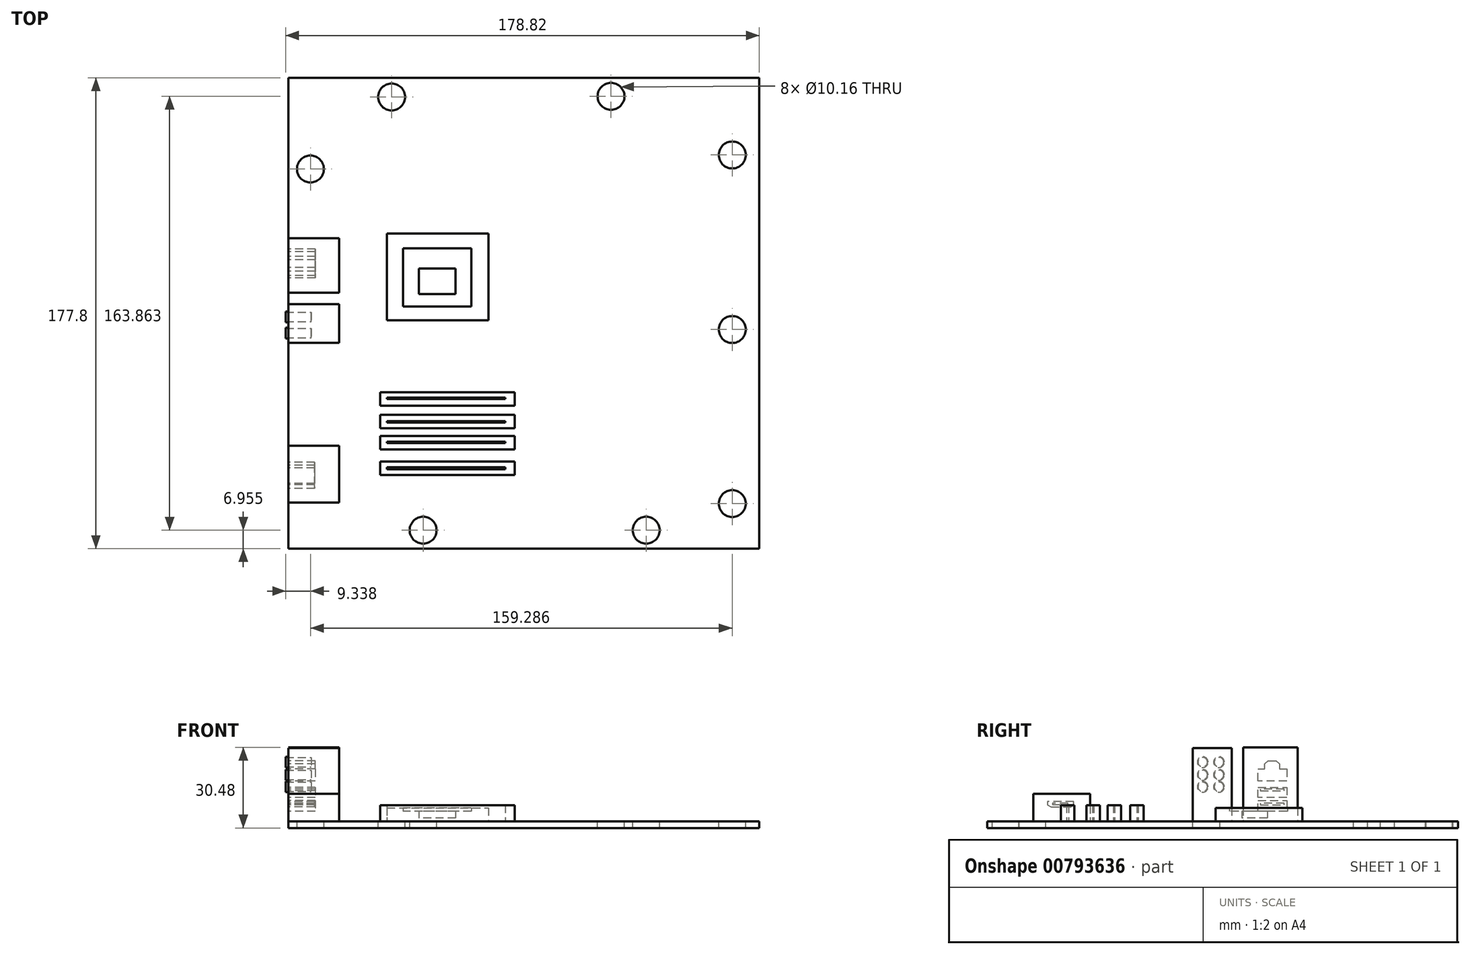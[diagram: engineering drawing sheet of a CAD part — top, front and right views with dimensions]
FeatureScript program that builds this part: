
annotation { "Feature Type Name" : "Feature", "Feature Type Description" : "" }
export const myFeature = defineFeature(function(context is Context, id is Id, definition is map)
    precondition{}
    {
        {
            var Q0;
            Q0=qCreatedBy(makeId("Top.planeOp"),FACE);
            var sketch = newSketch(context, id + "F0", { "sketchPlane" : qUnion([Q0])});
            skLineSegment(sketch, "E0", {"start": v(0, 177.8) * mm, "end": v(0, 0) * mm});
            skLineSegment(sketch, "E1", {"start": v(0, 0) * mm, "end": v(177.8, 0) * mm});
            skLineSegment(sketch, "E2", {"start": v(177.8, 0) * mm, "end": v(177.8, 177.8) * mm});
            skLineSegment(sketch, "E3", {"start": v(177.8, 177.8) * mm, "end": v(0, 177.8) * mm});
            skSolve(sketch);
        }
        {
            var Q0;
            Q0=makeQuery(id+"F0.imprint","IMPRINT",FACE,{"disambiguationData":[TD([[makeQuery(id+"F0.imprint","IMPRINT",EDGE,{"derivedFrom":sQuery(id+"F0.wireOp",EDGE,"E0")}),1.0]])]});
            extrude(context, id + "F1", {"entities" : qUnion([Q0]), "oppositeDirection" : true, "depth" : 2.54 * mm, "offsetDistance" : 25.4 * mm});
        }
        {
            var Q0;
            Q0=makeQuery(id+"F1.opExtrude","CAP_FACE",FACE,{"disambiguationData":[OSD([sQuery(id+"F0.wireOp",EDGE,"E0"),sQuery(id+"F0.wireOp",EDGE,"E1"),sQuery(id+"F0.wireOp",EDGE,"E2"),sQuery(id+"F0.wireOp",EDGE,"E3")])],"isStart":true});
            var sketch = newSketch(context, id + "F2", { "sketchPlane" : qUnion([Q0])});
            skLineSegment(sketch, "E4", {"start": v(0, 96.61) * mm, "end": v(0, 117.26) * mm});
            skLineSegment(sketch, "E5", {"start": v(0, 117.26) * mm, "end": v(19.18, 117.26) * mm});
            skLineSegment(sketch, "E6", {"start": v(19.18, 117.26) * mm, "end": v(19.18, 96.61) * mm});
            skLineSegment(sketch, "E7", {"start": v(19.18, 96.61) * mm, "end": v(0, 96.61) * mm});
            skSolve(sketch);
        }
        {
            var Q0;
            Q0 = qSketchRegion(id + "F2", true);
            extrude(context, id + "F3", {"entities" : qUnion([Q0]), "operationType" : NewBodyOperationType.ADD, "depth" : 27.94 * mm, "offsetDistance" : 25.4 * mm});
        }
        {
            var Q0;
            Q0=makeQuery(id+"F3.boolean.opBoolean","MERGE",FACE,{"derivedFrom":[makeQuery(id+"F1.opExtrude","SWEPT_FACE",FACE,{"disambiguationData":[OSD([sQuery(id+"F0.wireOp",EDGE,"E0")])]}),makeQuery(id+"F3.opExtrude","SWEPT_FACE",FACE,{"disambiguationData":[OSD([sQuery(id+"F2.wireOp",EDGE,"E4")])]})]});
            var sketch = newSketch(context, id + "F4", { "sketchPlane" : qUnion([Q0])});
            skLineSegment(sketch, "E8", {"start": v(-113.13, 3.74) * mm, "end": v(-102.3, 3.74) * mm});
            skLineSegment(sketch, "E9", {"start": v(-102.3, 3.74) * mm, "end": v(-102.3, 7.88) * mm});
            skLineSegment(sketch, "E10", {"start": v(-102.3, 7.88) * mm, "end": v(-113.13, 7.88) * mm});
            skLineSegment(sketch, "E11", {"start": v(-113.13, 7.88) * mm, "end": v(-113.13, 3.74) * mm});
            skLineSegment(sketch, "E12", {"start": v(-112.13, 6.81) * mm, "end": v(-103.18, 6.81) * mm});
            skLineSegment(sketch, "E13", {"start": v(-103.18, 6.81) * mm, "end": v(-103.18, 6.2) * mm});
            skLineSegment(sketch, "E14", {"start": v(-103.18, 6.2) * mm, "end": v(-112.13, 6.2) * mm});
            skLineSegment(sketch, "E15", {"start": v(-112.13, 6.2) * mm, "end": v(-112.13, 6.81) * mm});
            skLineSegment(sketch, "E16", {"start": v(-113.13, 8.95) * mm, "end": v(-102.3, 8.95) * mm});
            skLineSegment(sketch, "E17", {"start": v(-102.3, 8.95) * mm, "end": v(-102.3, 12.82) * mm});
            skLineSegment(sketch, "E18", {"start": v(-102.3, 12.82) * mm, "end": v(-113.13, 12.82) * mm});
            skLineSegment(sketch, "E19", {"start": v(-113.13, 12.82) * mm, "end": v(-113.13, 8.95) * mm});
            skLineSegment(sketch, "E20", {"start": v(-112.13, 12.1) * mm, "end": v(-103.18, 12.1) * mm});
            skPoint(sketch, "E20.endSnap0", {"position": v(-103.18, 6.5) * mm});
            skLineSegment(sketch, "E21", {"start": v(-103.18, 12.1) * mm, "end": v(-103.18, 11.52) * mm});
            skLineSegment(sketch, "E22", {"start": v(-103.18, 11.52) * mm, "end": v(-112.13, 11.52) * mm});
            skLineSegment(sketch, "E23", {"start": v(-112.13, 11.52) * mm, "end": v(-112.13, 12.1) * mm});
            skLineSegment(sketch, "E24", {"start": v(-113.13, 15.2) * mm, "end": v(-102.3, 15.2) * mm});
            skLineSegment(sketch, "E25", {"start": v(-102.3, 15.2) * mm, "end": v(-102.3, 19.75) * mm});
            skLineSegment(sketch, "E26", {"start": v(-102.3, 19.75) * mm, "end": v(-104.74, 19.75) * mm});
            skLineSegment(sketch, "E27", {"start": v(-104.74, 19.75) * mm, "end": v(-104.74, 21.69) * mm});
            skLineSegment(sketch, "E28", {"start": v(-104.74, 21.69) * mm, "end": v(-106.12, 22.8) * mm});
            skLineSegment(sketch, "E29", {"start": v(-106.12, 22.8) * mm, "end": v(-109.16, 22.8) * mm});
            skLineSegment(sketch, "E30", {"start": v(-109.16, 22.8) * mm, "end": v(-110.4, 21.69) * mm});
            skLineSegment(sketch, "E31", {"start": v(-110.4, 21.69) * mm, "end": v(-110.4, 19.75) * mm});
            skLineSegment(sketch, "E32", {"start": v(-110.4, 19.75) * mm, "end": v(-113.13, 19.75) * mm});
            skLineSegment(sketch, "E33", {"start": v(-113.13, 19.75) * mm, "end": v(-113.13, 15.2) * mm});
            skSolve(sketch);
        }
        {
            var Q0;
            Q0=makeQuery(id+"F4.imprint","IMPRINT",FACE,{"disambiguationData":[TD([[makeQuery(id+"F4.imprint","IMPRINT",EDGE,{"derivedFrom":sQuery(id+"F4.wireOp",EDGE,"E24")}),1.0]])]});
            var Q1;
            Q1=makeQuery(id+"F4.imprint","IMPRINT",FACE,{"disambiguationData":[TD([[makeQuery(id+"F4.imprint","IMPRINT",EDGE,{"derivedFrom":sQuery(id+"F4.wireOp",EDGE,"E16")}),1.0]])]});
            var Q2;
            Q2=makeQuery(id+"F4.imprint","IMPRINT",FACE,{"disambiguationData":[TD([[makeQuery(id+"F4.imprint","IMPRINT",EDGE,{"derivedFrom":sQuery(id+"F4.wireOp",EDGE,"E8")}),1.0]])]});
            extrude(context, id + "F5", {"entities" : qUnion([Q0, Q1, Q2]), "operationType" : NewBodyOperationType.REMOVE, "oppositeDirection" : true, "depth" : 10.16 * mm, "offsetDistance" : 25.4 * mm});
        }
        {
            var Q0;
            Q0=makeQuery(id+"F1.opExtrude","CAP_FACE",FACE,{"disambiguationData":[OSD([sQuery(id+"F0.wireOp",EDGE,"E0"),sQuery(id+"F0.wireOp",EDGE,"E1"),sQuery(id+"F0.wireOp",EDGE,"E2"),sQuery(id+"F0.wireOp",EDGE,"E3")])],"isStart":true});
            var sketch = newSketch(context, id + "F6", { "sketchPlane" : qUnion([Q0])});
            skLineSegment(sketch, "E34", {"start": v(0, 92.31) * mm, "end": v(19.18, 92.31) * mm});
            skLineSegment(sketch, "E35", {"start": v(19.18, 92.31) * mm, "end": v(19.18, 77.69) * mm});
            skLineSegment(sketch, "E36", {"start": v(19.18, 77.69) * mm, "end": v(0, 77.69) * mm});
            skSolve(sketch);
        }
        {
            var Q0;
            {var subQ0=sQuery(id+"F6.wireOp",EDGE,"E34");Q0=makeQuery(id+"F6.imprint","IMPRINT",FACE,{"disambiguationData":[TD([[makeQuery(id+"F6.imprint","IMPRINT",EDGE,{"derivedFrom":subQ0}),-1.0]])]});}
            extrude(context, id + "F7", {"entities" : qUnion([Q0]), "operationType" : NewBodyOperationType.ADD, "depth" : 27.7 * mm, "offsetDistance" : 25.4 * mm});
        }
        {
            var Q0;
            {var subQ0=sQuery(id+"F0.wireOp",EDGE,"E0");var subQ3=sQuery(id+"F0.wireOp",EDGE,"E1");var subQ6=sQuery(id+"F2.wireOp",EDGE,"E4");Q0=makeQuery(id+"F7.boolean.opBoolean","MERGE",FACE,{"derivedFrom":[makeQuery(id+"F5.boolean.opBoolean","SPLIT",FACE,{"disambiguationData":[TD([makeQuery(id+"F1.opExtrude","SWEPT_FACE",FACE,{"disambiguationData":[OSD([subQ3])]})])],"derivedFrom":makeQuery(id+"F3.boolean.opBoolean","MERGE",FACE,{"derivedFrom":[makeQuery(id+"F1.opExtrude","SWEPT_FACE",FACE,{"disambiguationData":[OSD([subQ0])]}),makeQuery(id+"F3.opExtrude","SWEPT_FACE",FACE,{"disambiguationData":[OSD([subQ6])]})]})}),makeQuery(id+"F7.opExtrude","SWEPT_FACE",FACE,{"disambiguationData":[OSD([subQ0])]})]});}
            var sketch = newSketch(context, id + "F8", { "sketchPlane" : qUnion([Q0])});
            skCircle(sketch, "E37", {"center": v(-81.39, 22.33) * mm, "radius": 1.78 * mm});
            skCircle(sketch, "E38", {"center": v(-87.55, 22.33) * mm, "radius": 1.78 * mm});
            skCircle(sketch, "E39", {"center": v(-87.55, 17.51) * mm, "radius": 1.78 * mm});
            skCircle(sketch, "E40", {"center": v(-81.39, 17.51) * mm, "radius": 1.78 * mm});
            skCircle(sketch, "E41", {"center": v(-81.39, 13) * mm, "radius": 1.78 * mm});
            skCircle(sketch, "E42", {"center": v(-87.55, 13) * mm, "radius": 1.78 * mm});
            skCircle(sketch, "E43", {"center": v(-87.55, 13) * mm, "radius": 2.03 * mm});
            skCircle(sketch, "E44", {"center": v(-81.39, 13) * mm, "radius": 2.03 * mm});
            skCircle(sketch, "E45", {"center": v(-81.39, 17.51) * mm, "radius": 2.03 * mm});
            skCircle(sketch, "E46", {"center": v(-87.55, 17.51) * mm, "radius": 2.03 * mm});
            skCircle(sketch, "E47", {"center": v(-87.55, 22.33) * mm, "radius": 2.03 * mm});
            skCircle(sketch, "E48", {"center": v(-81.39, 22.33) * mm, "radius": 2.03 * mm});
            skSolve(sketch);
        }
        {
            var Q0;
            Q0=makeQuery(id+"F8.imprint","IMPRINT",FACE,{"disambiguationData":[TD([[makeQuery(id+"F8.imprint","IMPRINT",EDGE,{"derivedFrom":sQuery(id+"F8.wireOp",EDGE,"E37")}),-1.0]])]});
            var Q1;
            Q1=makeQuery(id+"F8.imprint","IMPRINT",FACE,{"disambiguationData":[TD([[makeQuery(id+"F8.imprint","IMPRINT",EDGE,{"derivedFrom":sQuery(id+"F8.wireOp",EDGE,"E38")}),-1.0]])]});
            var Q2;
            Q2=makeQuery(id+"F8.imprint","IMPRINT",FACE,{"disambiguationData":[TD([[makeQuery(id+"F8.imprint","IMPRINT",EDGE,{"derivedFrom":sQuery(id+"F8.wireOp",EDGE,"E40")}),-1.0]])]});
            var Q3;
            Q3=makeQuery(id+"F8.imprint","IMPRINT",FACE,{"disambiguationData":[TD([[makeQuery(id+"F8.imprint","IMPRINT",EDGE,{"derivedFrom":sQuery(id+"F8.wireOp",EDGE,"E39")}),-1.0]])]});
            var Q4;
            Q4=makeQuery(id+"F8.imprint","IMPRINT",FACE,{"disambiguationData":[TD([[makeQuery(id+"F8.imprint","IMPRINT",EDGE,{"derivedFrom":sQuery(id+"F8.wireOp",EDGE,"E42")}),-1.0]])]});
            var Q5;
            Q5=makeQuery(id+"F8.imprint","IMPRINT",FACE,{"disambiguationData":[TD([[makeQuery(id+"F8.imprint","IMPRINT",EDGE,{"derivedFrom":sQuery(id+"F8.wireOp",EDGE,"E41")}),-1.0]])]});
            extrude(context, id + "F9", {"entities" : qUnion([Q0, Q1, Q2, Q3, Q4, Q5]), "operationType" : NewBodyOperationType.ADD, "depth" : 1.02 * mm, "offsetDistance" : 25.4 * mm});
        }
        {
            var Q0;
            {var subQ0=sQuery(id+"F0.wireOp",EDGE,"E0");var subQ3=sQuery(id+"F0.wireOp",EDGE,"E1");var subQ6=sQuery(id+"F2.wireOp",EDGE,"E4");Q0=makeQuery(id+"F9.boolean.opBoolean","SPLIT",FACE,{"disambiguationData":[TD([makeQuery(id+"F9.opExtrude","SWEPT_FACE",FACE,{"disambiguationData":[OSD([sQuery(id+"F8.wireOp",EDGE,"E38")])]})])],"derivedFrom":makeQuery(id+"F7.boolean.opBoolean","MERGE",FACE,{"derivedFrom":[makeQuery(id+"F5.boolean.opBoolean","SPLIT",FACE,{"disambiguationData":[TD([makeQuery(id+"F1.opExtrude","SWEPT_FACE",FACE,{"disambiguationData":[OSD([subQ3])]})])],"derivedFrom":makeQuery(id+"F3.boolean.opBoolean","MERGE",FACE,{"derivedFrom":[makeQuery(id+"F1.opExtrude","SWEPT_FACE",FACE,{"disambiguationData":[OSD([subQ0])]}),makeQuery(id+"F3.opExtrude","SWEPT_FACE",FACE,{"disambiguationData":[OSD([subQ6])]})]})}),makeQuery(id+"F7.opExtrude","SWEPT_FACE",FACE,{"disambiguationData":[OSD([subQ0])]})]})});}
            var Q1;
            {var subQ0=sQuery(id+"F0.wireOp",EDGE,"E0");var subQ3=sQuery(id+"F0.wireOp",EDGE,"E1");var subQ6=sQuery(id+"F2.wireOp",EDGE,"E4");Q1=makeQuery(id+"F9.boolean.opBoolean","SPLIT",FACE,{"disambiguationData":[TD([makeQuery(id+"F9.opExtrude","SWEPT_FACE",FACE,{"disambiguationData":[OSD([sQuery(id+"F8.wireOp",EDGE,"E37")])]})])],"derivedFrom":makeQuery(id+"F7.boolean.opBoolean","MERGE",FACE,{"derivedFrom":[makeQuery(id+"F5.boolean.opBoolean","SPLIT",FACE,{"disambiguationData":[TD([makeQuery(id+"F1.opExtrude","SWEPT_FACE",FACE,{"disambiguationData":[OSD([subQ3])]})])],"derivedFrom":makeQuery(id+"F3.boolean.opBoolean","MERGE",FACE,{"derivedFrom":[makeQuery(id+"F1.opExtrude","SWEPT_FACE",FACE,{"disambiguationData":[OSD([subQ0])]}),makeQuery(id+"F3.opExtrude","SWEPT_FACE",FACE,{"disambiguationData":[OSD([subQ6])]})]})}),makeQuery(id+"F7.opExtrude","SWEPT_FACE",FACE,{"disambiguationData":[OSD([subQ0])]})]})});}
            var Q2;
            {var subQ0=sQuery(id+"F0.wireOp",EDGE,"E0");var subQ3=sQuery(id+"F0.wireOp",EDGE,"E1");var subQ6=sQuery(id+"F2.wireOp",EDGE,"E4");Q2=makeQuery(id+"F9.boolean.opBoolean","SPLIT",FACE,{"disambiguationData":[TD([makeQuery(id+"F9.opExtrude","SWEPT_FACE",FACE,{"disambiguationData":[OSD([sQuery(id+"F8.wireOp",EDGE,"E40")])]})])],"derivedFrom":makeQuery(id+"F7.boolean.opBoolean","MERGE",FACE,{"derivedFrom":[makeQuery(id+"F5.boolean.opBoolean","SPLIT",FACE,{"disambiguationData":[TD([makeQuery(id+"F1.opExtrude","SWEPT_FACE",FACE,{"disambiguationData":[OSD([subQ3])]})])],"derivedFrom":makeQuery(id+"F3.boolean.opBoolean","MERGE",FACE,{"derivedFrom":[makeQuery(id+"F1.opExtrude","SWEPT_FACE",FACE,{"disambiguationData":[OSD([subQ0])]}),makeQuery(id+"F3.opExtrude","SWEPT_FACE",FACE,{"disambiguationData":[OSD([subQ6])]})]})}),makeQuery(id+"F7.opExtrude","SWEPT_FACE",FACE,{"disambiguationData":[OSD([subQ0])]})]})});}
            var Q3;
            {var subQ0=sQuery(id+"F0.wireOp",EDGE,"E0");var subQ3=sQuery(id+"F0.wireOp",EDGE,"E1");var subQ6=sQuery(id+"F2.wireOp",EDGE,"E4");Q3=makeQuery(id+"F9.boolean.opBoolean","SPLIT",FACE,{"disambiguationData":[TD([makeQuery(id+"F9.opExtrude","SWEPT_FACE",FACE,{"disambiguationData":[OSD([sQuery(id+"F8.wireOp",EDGE,"E39")])]})])],"derivedFrom":makeQuery(id+"F7.boolean.opBoolean","MERGE",FACE,{"derivedFrom":[makeQuery(id+"F5.boolean.opBoolean","SPLIT",FACE,{"disambiguationData":[TD([makeQuery(id+"F1.opExtrude","SWEPT_FACE",FACE,{"disambiguationData":[OSD([subQ3])]})])],"derivedFrom":makeQuery(id+"F3.boolean.opBoolean","MERGE",FACE,{"derivedFrom":[makeQuery(id+"F1.opExtrude","SWEPT_FACE",FACE,{"disambiguationData":[OSD([subQ0])]}),makeQuery(id+"F3.opExtrude","SWEPT_FACE",FACE,{"disambiguationData":[OSD([subQ6])]})]})}),makeQuery(id+"F7.opExtrude","SWEPT_FACE",FACE,{"disambiguationData":[OSD([subQ0])]})]})});}
            var Q4;
            {var subQ0=sQuery(id+"F0.wireOp",EDGE,"E0");var subQ3=sQuery(id+"F0.wireOp",EDGE,"E1");var subQ6=sQuery(id+"F2.wireOp",EDGE,"E4");Q4=makeQuery(id+"F9.boolean.opBoolean","SPLIT",FACE,{"disambiguationData":[TD([makeQuery(id+"F9.opExtrude","SWEPT_FACE",FACE,{"disambiguationData":[OSD([sQuery(id+"F8.wireOp",EDGE,"E42")])]})])],"derivedFrom":makeQuery(id+"F7.boolean.opBoolean","MERGE",FACE,{"derivedFrom":[makeQuery(id+"F5.boolean.opBoolean","SPLIT",FACE,{"disambiguationData":[TD([makeQuery(id+"F1.opExtrude","SWEPT_FACE",FACE,{"disambiguationData":[OSD([subQ3])]})])],"derivedFrom":makeQuery(id+"F3.boolean.opBoolean","MERGE",FACE,{"derivedFrom":[makeQuery(id+"F1.opExtrude","SWEPT_FACE",FACE,{"disambiguationData":[OSD([subQ0])]}),makeQuery(id+"F3.opExtrude","SWEPT_FACE",FACE,{"disambiguationData":[OSD([subQ6])]})]})}),makeQuery(id+"F7.opExtrude","SWEPT_FACE",FACE,{"disambiguationData":[OSD([subQ0])]})]})});}
            var Q5;
            {var subQ0=sQuery(id+"F0.wireOp",EDGE,"E0");var subQ3=sQuery(id+"F0.wireOp",EDGE,"E1");var subQ6=sQuery(id+"F2.wireOp",EDGE,"E4");Q5=makeQuery(id+"F9.boolean.opBoolean","SPLIT",FACE,{"disambiguationData":[TD([makeQuery(id+"F9.opExtrude","SWEPT_FACE",FACE,{"disambiguationData":[OSD([sQuery(id+"F8.wireOp",EDGE,"E41")])]})])],"derivedFrom":makeQuery(id+"F7.boolean.opBoolean","MERGE",FACE,{"derivedFrom":[makeQuery(id+"F5.boolean.opBoolean","SPLIT",FACE,{"disambiguationData":[TD([makeQuery(id+"F1.opExtrude","SWEPT_FACE",FACE,{"disambiguationData":[OSD([subQ3])]})])],"derivedFrom":makeQuery(id+"F3.boolean.opBoolean","MERGE",FACE,{"derivedFrom":[makeQuery(id+"F1.opExtrude","SWEPT_FACE",FACE,{"disambiguationData":[OSD([subQ0])]}),makeQuery(id+"F3.opExtrude","SWEPT_FACE",FACE,{"disambiguationData":[OSD([subQ6])]})]})}),makeQuery(id+"F7.opExtrude","SWEPT_FACE",FACE,{"disambiguationData":[OSD([subQ0])]})]})});}
            extrude(context, id + "F10", {"entities" : qUnion([Q0, Q1, Q2, Q3, Q4, Q5]), "operationType" : NewBodyOperationType.REMOVE, "oppositeDirection" : true, "depth" : 8.64 * mm, "offsetDistance" : 25.4 * mm});
        }
        {
            var Q0;
            Q0=makeQuery(id+"F1.opExtrude","CAP_FACE",FACE,{"disambiguationData":[OSD([sQuery(id+"F0.wireOp",EDGE,"E0"),sQuery(id+"F0.wireOp",EDGE,"E1"),sQuery(id+"F0.wireOp",EDGE,"E2"),sQuery(id+"F0.wireOp",EDGE,"E3")])],"isStart":true});
            var sketch = newSketch(context, id + "F11", { "sketchPlane" : qUnion([Q0])});
            skLineSegment(sketch, "E49", {"start": v(0, 38.84) * mm, "end": v(19.18, 38.84) * mm});
            skLineSegment(sketch, "E50", {"start": v(19.18, 38.84) * mm, "end": v(19.18, 17.46) * mm});
            skLineSegment(sketch, "E51", {"start": v(19.18, 17.46) * mm, "end": v(0, 17.46) * mm});
            skSolve(sketch);
        }
        {
            var Q0;
            {var subQ0=sQuery(id+"F11.wireOp",EDGE,"E49");Q0=makeQuery(id+"F11.imprint","IMPRINT",FACE,{"disambiguationData":[TD([[makeQuery(id+"F11.imprint","IMPRINT",EDGE,{"derivedFrom":subQ0}),-1.0]])]});}
            extrude(context, id + "F12", {"entities" : qUnion([Q0]), "operationType" : NewBodyOperationType.ADD, "depth" : 10.4 * mm, "offsetDistance" : 25.4 * mm});
        }
        {
            var Q0;
            {var subQ0=sQuery(id+"F0.wireOp",EDGE,"E0");var subQ6=sQuery(id+"F2.wireOp",EDGE,"E4");var subQ15=sQuery(id+"F0.wireOp",EDGE,"E1");var subQ27=makeQuery(id+"F1.opExtrude","SWEPT_FACE",FACE,{"disambiguationData":[OSD([subQ15])]});Q0=makeQuery(id+"F12.boolean.opBoolean","MERGE",FACE,{"derivedFrom":[makeQuery(id+"F9.boolean.opBoolean","SPLIT",FACE,{"disambiguationData":[TD([subQ27])],"derivedFrom":makeQuery(id+"F7.boolean.opBoolean","MERGE",FACE,{"derivedFrom":[makeQuery(id+"F5.boolean.opBoolean","SPLIT",FACE,{"disambiguationData":[TD([subQ27])],"derivedFrom":makeQuery(id+"F3.boolean.opBoolean","MERGE",FACE,{"derivedFrom":[makeQuery(id+"F1.opExtrude","SWEPT_FACE",FACE,{"disambiguationData":[OSD([subQ0])]}),makeQuery(id+"F3.opExtrude","SWEPT_FACE",FACE,{"disambiguationData":[OSD([subQ6])]})]})}),makeQuery(id+"F7.opExtrude","SWEPT_FACE",FACE,{"disambiguationData":[OSD([subQ0])]})]})}),makeQuery(id+"F12.opExtrude","SWEPT_FACE",FACE,{"disambiguationData":[OSD([subQ0])]})]});}
            var sketch = newSketch(context, id + "F13", { "sketchPlane" : qUnion([Q0])});
            skLineSegment(sketch, "E52", {"start": v(-32.39, 7.45) * mm, "end": v(-22.77, 7.45) * mm});
            skLineSegment(sketch, "E53", {"start": v(-22.77, 7.45) * mm, "end": v(-22.77, 6.18) * mm});
            skLineSegment(sketch, "E54", {"start": v(-22.77, 6.18) * mm, "end": v(-24.14, 5.45) * mm});
            skLineSegment(sketch, "E55", {"start": v(-24.14, 5.45) * mm, "end": v(-31.46, 5.45) * mm});
            skLineSegment(sketch, "E56", {"start": v(-31.46, 5.45) * mm, "end": v(-32.63, 6.23) * mm});
            skLineSegment(sketch, "E57", {"start": v(-32.63, 6.23) * mm, "end": v(-32.63, 7.45) * mm});
            skLineSegment(sketch, "E58", {"start": v(-30.44, 6.8) * mm, "end": v(-24.7, 6.8) * mm});
            skLineSegment(sketch, "E59", {"start": v(-24.7, 6.8) * mm, "end": v(-24.7, 6.3) * mm});
            skLineSegment(sketch, "E60", {"start": v(-24.7, 6.3) * mm, "end": v(-30.44, 6.3) * mm});
            skLineSegment(sketch, "E61", {"start": v(-30.44, 6.3) * mm, "end": v(-30.44, 6.8) * mm});
            skLineSegment(sketch, "E62", {"start": v(-32.39, 7.45) * mm, "end": v(-32.63, 7.45) * mm});
            skSolve(sketch);
        }
        {
            var Q0;
            Q0=makeQuery(id+"F13.imprint","IMPRINT",FACE,{"disambiguationData":[TD([[makeQuery(id+"F13.imprint","IMPRINT",EDGE,{"derivedFrom":sQuery(id+"F13.wireOp",EDGE,"E52")}),-1.0]])]});
            extrude(context, id + "F14", {"entities" : qUnion([Q0]), "operationType" : NewBodyOperationType.REMOVE, "oppositeDirection" : true, "depth" : 9.9 * mm, "offsetDistance" : 25.4 * mm});
        }
        {
            var Q0;
            Q0=makeQuery(id+"F1.opExtrude","CAP_FACE",FACE,{"disambiguationData":[OSD([sQuery(id+"F0.wireOp",EDGE,"E0"),sQuery(id+"F0.wireOp",EDGE,"E1"),sQuery(id+"F0.wireOp",EDGE,"E2"),sQuery(id+"F0.wireOp",EDGE,"E3")])],"isStart":true});
            var sketch = newSketch(context, id + "F15", { "sketchPlane" : qUnion([Q0])});
            skCircle(sketch, "E63", {"center": v(38.97, 170.6) * mm, "radius": 5.08 * mm});
            skCircle(sketch, "E64", {"center": v(121.83, 170.82) * mm, "radius": 5.08 * mm});
            skCircle(sketch, "E65", {"center": v(167.6, 148.68) * mm, "radius": 5.08 * mm});
            skCircle(sketch, "E66", {"center": v(167.6, 82.77) * mm, "radius": 5.08 * mm});
            skCircle(sketch, "E67", {"center": v(167.6, 17.02) * mm, "radius": 5.08 * mm});
            skCircle(sketch, "E68", {"center": v(135.1, 6.95) * mm, "radius": 5.08 * mm});
            skCircle(sketch, "E69", {"center": v(50.89, 6.95) * mm, "radius": 5.08 * mm});
            skCircle(sketch, "E70", {"center": v(8.32, 143.36) * mm, "radius": 5.08 * mm});
            skSolve(sketch);
        }
        {
            var Q0;
            Q0=makeQuery(id+"F15.imprint","IMPRINT",FACE,{"disambiguationData":[TD([[makeQuery(id+"F15.imprint","IMPRINT",EDGE,{"derivedFrom":sQuery(id+"F15.wireOp",EDGE,"E70")}),1.0]])]});
            var Q1;
            Q1=makeQuery(id+"F15.imprint","IMPRINT",FACE,{"disambiguationData":[TD([[makeQuery(id+"F15.imprint","IMPRINT",EDGE,{"derivedFrom":sQuery(id+"F15.wireOp",EDGE,"E63")}),1.0]])]});
            var Q2;
            Q2=makeQuery(id+"F15.imprint","IMPRINT",FACE,{"disambiguationData":[TD([[makeQuery(id+"F15.imprint","IMPRINT",EDGE,{"derivedFrom":sQuery(id+"F15.wireOp",EDGE,"E64")}),1.0]])]});
            var Q3;
            Q3=makeQuery(id+"F15.imprint","IMPRINT",FACE,{"disambiguationData":[TD([[makeQuery(id+"F15.imprint","IMPRINT",EDGE,{"derivedFrom":sQuery(id+"F15.wireOp",EDGE,"E65")}),1.0]])]});
            var Q4;
            Q4=makeQuery(id+"F15.imprint","IMPRINT",FACE,{"disambiguationData":[TD([[makeQuery(id+"F15.imprint","IMPRINT",EDGE,{"derivedFrom":sQuery(id+"F15.wireOp",EDGE,"E66")}),1.0]])]});
            var Q5;
            Q5=makeQuery(id+"F15.imprint","IMPRINT",FACE,{"disambiguationData":[TD([[makeQuery(id+"F15.imprint","IMPRINT",EDGE,{"derivedFrom":sQuery(id+"F15.wireOp",EDGE,"E67")}),1.0]])]});
            var Q6;
            Q6=makeQuery(id+"F15.imprint","IMPRINT",FACE,{"disambiguationData":[TD([[makeQuery(id+"F15.imprint","IMPRINT",EDGE,{"derivedFrom":sQuery(id+"F15.wireOp",EDGE,"E68")}),1.0]])]});
            var Q7;
            Q7=makeQuery(id+"F15.imprint","IMPRINT",FACE,{"disambiguationData":[TD([[makeQuery(id+"F15.imprint","IMPRINT",EDGE,{"derivedFrom":sQuery(id+"F15.wireOp",EDGE,"E69")}),1.0]])]});
            extrude(context, id + "F16", {"entities" : qUnion([Q0, Q1, Q2, Q3, Q4, Q5, Q6, Q7]), "operationType" : NewBodyOperationType.REMOVE, "oppositeDirection" : true, "depth" : 2.54 * mm, "offsetDistance" : 25.4 * mm});
        }
        {
            var Q0;
            Q0=makeQuery(id+"F1.opExtrude","CAP_FACE",FACE,{"disambiguationData":[OSD([sQuery(id+"F0.wireOp",EDGE,"E0"),sQuery(id+"F0.wireOp",EDGE,"E1"),sQuery(id+"F0.wireOp",EDGE,"E2"),sQuery(id+"F0.wireOp",EDGE,"E3")])],"isStart":true});
            var sketch = newSketch(context, id + "F17", { "sketchPlane" : qUnion([Q0])});
            skLineSegment(sketch, "E71", {"start": v(37.25, 118.98) * mm, "end": v(75.53, 118.98) * mm});
            skLineSegment(sketch, "E72", {"start": v(75.53, 118.98) * mm, "end": v(75.53, 86.29) * mm});
            skLineSegment(sketch, "E73", {"start": v(75.53, 86.29) * mm, "end": v(37.25, 86.29) * mm});
            skLineSegment(sketch, "E74", {"start": v(37.25, 86.29) * mm, "end": v(37.25, 118.98) * mm});
            skLineSegment(sketch, "E75", {"start": v(43.27, 113.39) * mm, "end": v(43.27, 91.45) * mm});
            skLineSegment(sketch, "E76", {"start": v(43.27, 91.45) * mm, "end": v(69.08, 91.45) * mm});
            skLineSegment(sketch, "E77", {"start": v(69.08, 91.45) * mm, "end": v(69.08, 113.39) * mm});
            skLineSegment(sketch, "E78", {"start": v(69.08, 113.39) * mm, "end": v(43.27, 113.39) * mm});
            skLineSegment(sketch, "E79", {"start": v(49.26, 105.82) * mm, "end": v(49.26, 96.12) * mm});
            skLineSegment(sketch, "E80", {"start": v(49.26, 96.12) * mm, "end": v(63.16, 96.12) * mm});
            skLineSegment(sketch, "E81", {"start": v(63.16, 96.12) * mm, "end": v(63.16, 105.82) * mm});
            skLineSegment(sketch, "E82", {"start": v(63.16, 105.82) * mm, "end": v(49.26, 105.82) * mm});
            skSolve(sketch);
        }
        {
            var Q0;
            Q0=makeQuery(id+"F17.imprint","IMPRINT",FACE,{"disambiguationData":[TD([[makeQuery(id+"F17.imprint","IMPRINT",EDGE,{"derivedFrom":sQuery(id+"F17.wireOp",EDGE,"E71")}),-1.0]])]});
            extrude(context, id + "F18", {"entities" : qUnion([Q0]), "operationType" : NewBodyOperationType.ADD, "depth" : 5.08 * mm, "offsetDistance" : 25.4 * mm});
        }
        {
            var Q0;
            Q0=makeQuery(id+"F17.imprint","IMPRINT",FACE,{"disambiguationData":[TD([[makeQuery(id+"F17.imprint","IMPRINT",EDGE,{"derivedFrom":sQuery(id+"F17.wireOp",EDGE,"E75")}),1.0]])]});
            extrude(context, id + "F19", {"entities" : qUnion([Q0]), "operationType" : NewBodyOperationType.ADD, "depth" : 3.8 * mm, "offsetDistance" : 25.4 * mm});
        }
        {
            var Q0;
            Q0=makeQuery(id+"F18.boolean.opBoolean","SPLIT",FACE,{"disambiguationData":[TD([makeQuery(id+"F18.opExtrude","SWEPT_FACE",FACE,{"disambiguationData":[OSD([sQuery(id+"F17.wireOp",EDGE,"E75")])]})])],"derivedFrom":makeQuery(id+"F1.opExtrude","CAP_FACE",FACE,{"disambiguationData":[OSD([sQuery(id+"F0.wireOp",EDGE,"E0"),sQuery(id+"F0.wireOp",EDGE,"E1"),sQuery(id+"F0.wireOp",EDGE,"E2"),sQuery(id+"F0.wireOp",EDGE,"E3")])],"isStart":true})});
            extrude(context, id + "F20", {"entities" : qUnion([Q0]), "operationType" : NewBodyOperationType.ADD, "depth" : 1.27 * mm, "offsetDistance" : 25.4 * mm});
        }
        {
            var Q0;
            {var subQ0=sQuery(id+"F0.wireOp",EDGE,"E1");var subQ1=sQuery(id+"F0.wireOp",EDGE,"E0");var subQ2=sQuery(id+"F0.wireOp",EDGE,"E3");var subQ3=sQuery(id+"F0.wireOp",EDGE,"E2");Q0=makeQuery(id+"F18.boolean.opBoolean","SPLIT",FACE,{"disambiguationData":[TD([makeQuery(id+"F1.opExtrude","SWEPT_FACE",FACE,{"disambiguationData":[OSD([subQ1])]})])],"derivedFrom":makeQuery(id+"F1.opExtrude","CAP_FACE",FACE,{"disambiguationData":[OSD([subQ1,subQ0,subQ3,subQ2])],"isStart":true})});}
            var sketch = newSketch(context, id + "F21", { "sketchPlane" : qUnion([Q0])});
            skLineSegment(sketch, "E83", {"start": v(34.65, 59.05) * mm, "end": v(85.45, 59.05) * mm});
            skLineSegment(sketch, "E84", {"start": v(85.45, 59.05) * mm, "end": v(85.45, 53.97) * mm});
            skLineSegment(sketch, "E85", {"start": v(85.45, 53.97) * mm, "end": v(34.65, 53.97) * mm});
            skLineSegment(sketch, "E86", {"start": v(34.65, 53.97) * mm, "end": v(34.65, 59.05) * mm});
            skLineSegment(sketch, "E87", {"start": v(34.65, 50.52) * mm, "end": v(85.45, 50.52) * mm});
            skLineSegment(sketch, "E88", {"start": v(85.45, 50.52) * mm, "end": v(85.45, 45.44) * mm});
            skLineSegment(sketch, "E89", {"start": v(85.45, 45.44) * mm, "end": v(34.65, 45.44) * mm});
            skLineSegment(sketch, "E90", {"start": v(34.65, 45.44) * mm, "end": v(34.65, 50.52) * mm});
            skLineSegment(sketch, "E91", {"start": v(34.65, 42.56) * mm, "end": v(85.45, 42.56) * mm});
            skLineSegment(sketch, "E92", {"start": v(85.45, 42.56) * mm, "end": v(85.45, 37.48) * mm});
            skLineSegment(sketch, "E93", {"start": v(85.45, 37.48) * mm, "end": v(34.65, 37.48) * mm});
            skLineSegment(sketch, "E94", {"start": v(34.65, 37.48) * mm, "end": v(34.65, 42.56) * mm});
            skLineSegment(sketch, "E95", {"start": v(34.65, 32.9) * mm, "end": v(85.45, 32.9) * mm});
            skLineSegment(sketch, "E96", {"start": v(85.45, 32.9) * mm, "end": v(85.45, 27.81) * mm});
            skLineSegment(sketch, "E97", {"start": v(85.45, 27.81) * mm, "end": v(34.65, 27.81) * mm});
            skLineSegment(sketch, "E98", {"start": v(34.65, 27.81) * mm, "end": v(34.65, 32.9) * mm});
            skLineSegment(sketch, "E99", {"start": v(37.25, 57) * mm, "end": v(81.88, 57) * mm});
            skLineSegment(sketch, "E100", {"start": v(81.88, 57) * mm, "end": v(81.88, 56.5) * mm});
            skLineSegment(sketch, "E101", {"start": v(81.88, 56.5) * mm, "end": v(37.25, 56.5) * mm});
            skLineSegment(sketch, "E102", {"start": v(37.25, 56.5) * mm, "end": v(37.25, 57) * mm});
            skLineSegment(sketch, "E103", {"start": v(37.25, 48.18) * mm, "end": v(81.88, 48.18) * mm});
            skLineSegment(sketch, "E104", {"start": v(81.88, 48.18) * mm, "end": v(81.88, 47.68) * mm});
            skLineSegment(sketch, "E105", {"start": v(81.88, 47.68) * mm, "end": v(37.25, 47.68) * mm});
            skLineSegment(sketch, "E106", {"start": v(37.25, 47.68) * mm, "end": v(37.25, 48.18) * mm});
            skLineSegment(sketch, "E107", {"start": v(37.25, 40.33) * mm, "end": v(81.88, 40.33) * mm});
            skLineSegment(sketch, "E108", {"start": v(81.88, 40.33) * mm, "end": v(81.88, 39.84) * mm});
            skLineSegment(sketch, "E109", {"start": v(81.88, 39.84) * mm, "end": v(37.25, 39.84) * mm});
            skLineSegment(sketch, "E110", {"start": v(37.25, 39.84) * mm, "end": v(37.25, 40.33) * mm});
            skLineSegment(sketch, "E111", {"start": v(37.25, 30.7) * mm, "end": v(81.88, 30.7) * mm});
            skLineSegment(sketch, "E112", {"start": v(81.88, 30.7) * mm, "end": v(81.88, 29.96) * mm});
            skLineSegment(sketch, "E113", {"start": v(81.88, 29.96) * mm, "end": v(37.25, 29.96) * mm});
            skLineSegment(sketch, "E114", {"start": v(37.25, 29.96) * mm, "end": v(37.25, 30.7) * mm});
            skSolve(sketch);
        }
        {
            var Q0;
            Q0=makeQuery(id+"F21.imprint","IMPRINT",FACE,{"disambiguationData":[TD([[makeQuery(id+"F21.imprint","IMPRINT",EDGE,{"derivedFrom":sQuery(id+"F21.wireOp",EDGE,"E83")}),-1.0]])]});
            var Q1;
            Q1=makeQuery(id+"F21.imprint","IMPRINT",FACE,{"disambiguationData":[TD([[makeQuery(id+"F21.imprint","IMPRINT",EDGE,{"derivedFrom":sQuery(id+"F21.wireOp",EDGE,"E87")}),-1.0]])]});
            var Q2;
            Q2=makeQuery(id+"F21.imprint","IMPRINT",FACE,{"disambiguationData":[TD([[makeQuery(id+"F21.imprint","IMPRINT",EDGE,{"derivedFrom":sQuery(id+"F21.wireOp",EDGE,"E91")}),-1.0]])]});
            var Q3;
            Q3=makeQuery(id+"F21.imprint","IMPRINT",FACE,{"disambiguationData":[TD([[makeQuery(id+"F21.imprint","IMPRINT",EDGE,{"derivedFrom":sQuery(id+"F21.wireOp",EDGE,"E95")}),-1.0]])]});
            extrude(context, id + "F22", {"entities" : qUnion([Q0, Q1, Q2, Q3]), "operationType" : NewBodyOperationType.ADD, "depth" : 6.1 * mm, "offsetDistance" : 25.4 * mm});
        }
    });
